# Revit family: Eye_Face_Wash-Acorn-Recessed_Swing_Down-S0560
name_source: partatom
category: Plumbing Fixtures
revit_build: Autodesk Revit 2018 (Build: 20170223_1515(x64)
units: mm (PartAtom-declared; Revit-internal decimal feet)

## family parameters
Cut with Voids When Loaded = Yes
Host = Face
OmniClass Number = 23.45.05.14.24
OmniClass Title = Eye Wash Fountains
Part Type = Normal
Room Calculation Point = No
Round Connector Dimension = Use Diameter
Shared = Yes

## types (1)
- S0560
    ADA Compliant = Yes
    Assembly Code = D2090900
    CW Connection = Yes
    CWFU = 3
    Cold Water Connection Diameter = 1/2"
    Cold Water Connection Radius = 1/4"
    Default Elevation = 0"
    Description = Swing Down Eye/Face Wash
Model S0560 is a recessed, wall mounted swing down eye/face wash that is installed in the wall with a stainless steel cabinet and ABS plastic eye/face wash spray heads. The eye/face wash swings down horizontally and the water flow is activated automatically. The eye/face wash flow is terminated once the unit has been swung back up into the cabinet for storage.
    Finish = Metal-Acorn-Stainless Steel
    HW Connection = No
    HWFU = 3
    Height = 33 1/4"
    Installation Type = Recessed
    Length = 4 1/8"
    Manufacturer = Acorn
    Material = Metal-Acorn-Stainless Steel
    Model = S0560
    Mounting Height = 33"
    Mounting Height Constraint = 33"
    Price = Prices may vary. Please consult Manufacturer Representative for most up-to-date price list.
    Product Documentation Link = https://www.acorneng.com
    Product Page URL = https://www.acorneng.com
    URL = https://www.acorneng.com
    Vent Connection = No
    WFU = 4
    Wash Head Finish = ABS Plastic-Acorn-Yellow
    Waste Connection = No
    Width = 18 3/8"

## geometry (parser evidence)
native form markers: Sweep x2
no freeform markers — native parametric forms only
